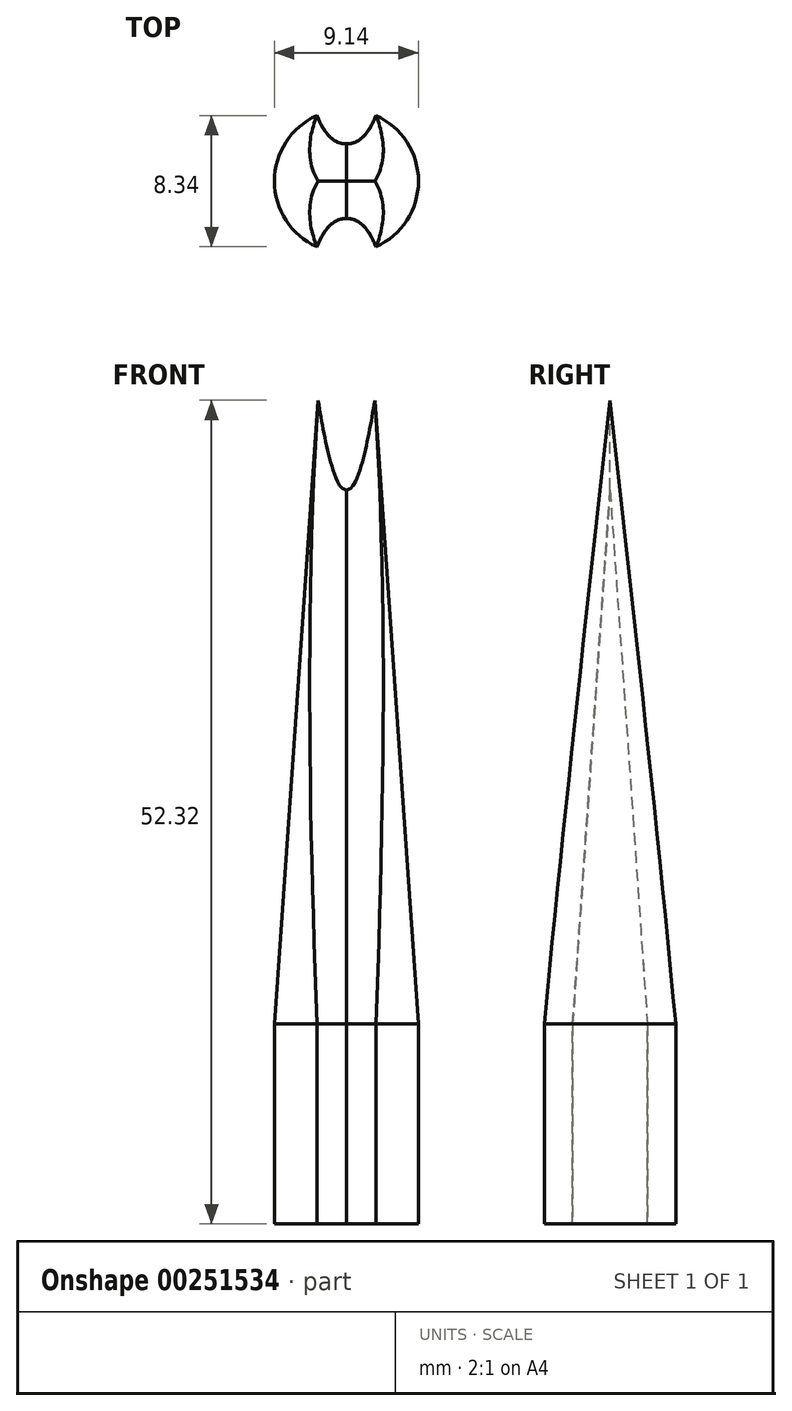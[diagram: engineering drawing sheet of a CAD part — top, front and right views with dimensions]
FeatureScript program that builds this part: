
annotation { "Feature Type Name" : "Feature", "Feature Type Description" : "" }
export const myFeature = defineFeature(function(context is Context, id is Id, definition is map)
    precondition{}
    {
        {
            var Q0;
            Q0=qCreatedBy(makeId("Top.planeOp"),FACE);
            var sketch = newSketch(context, id + "F0", { "sketchPlane" : qUnion([Q0])});
            skArc(sketch, "E0", {"start": v(-1.87, 4.17) * mm, "mid": v(-4.57, 0) * mm, "end": v(-1.87, -4.17) * mm});
            skFitSpline(sketch, "E1", {"points": [v(-1.87, 4.17) * mm, v(0, 2.37) * mm], "startDerivative": vector(1, -2.54) * mm, "endDerivative": vector(2.94, 0.07) * mm});
            skFitSpline(sketch, "E2.MirrorCS", {"points": [v(1.87, 4.17) * mm, v(0, 2.37) * mm], "startDerivative": vector(-1, -2.54) * mm, "endDerivative": vector(-2.94, 0.07) * mm});
            skFitSpline(sketch, "E3.MirrorCS", {"points": [v(-1.87, -4.17) * mm, v(0, -2.37) * mm], "startDerivative": vector(1, 2.54) * mm, "endDerivative": vector(2.94, -0.07) * mm});
            skFitSpline(sketch, "E4.MirrorCS", {"points": [v(1.87, -4.17) * mm, v(0, -2.37) * mm], "startDerivative": vector(-1, 2.54) * mm, "endDerivative": vector(-2.94, -0.07) * mm});
            skFitSpline(sketch, "E5.MirrorCS", {"points": [v(-1.87, -4.17) * mm, v(0, -2.37) * mm], "startDerivative": vector(1, 2.54) * mm, "endDerivative": vector(2.94, -0.07) * mm});
            skArc(sketch, "E6.trimOffspring", {"start": v(1.87, -4.17) * mm, "mid": v(4.57, 0) * mm, "end": v(1.87, 4.17) * mm});
            skSolve(sketch);
        }
        {
            var Q0;
            Q0=makeQuery(id+"F0.imprint","IMPRINT",FACE,{"disambiguationData":[TD([[makeQuery(id+"F0.imprint","IMPRINT",EDGE,{"derivedFrom":sQuery(id+"F0.wireOp",EDGE,"E0")}),1.0]])]});
            extrude(context, id + "F1", {"entities" : qUnion([Q0]), "depth" : 40.9 * mm, "hasDraft" : true, "draftAngle" : 4 * degree, "draftPullDirection" : true});
        }
        {
            var Q0;
            Q0=makeQuery(id+"F1.opExtrude","CAP_FACE",FACE,{"disambiguationData":[OSD([sQuery(id+"F0.wireOp",EDGE,"E0"),sQuery(id+"F0.wireOp",EDGE,"E1"),sQuery(id+"F0.wireOp",EDGE,"E2.MirrorCS"),sQuery(id+"F0.wireOp",EDGE,"E4.MirrorCS"),sQuery(id+"F0.wireOp",EDGE,"E5.MirrorCS"),sQuery(id+"F0.wireOp",EDGE,"E6.trimOffspring")])],"isStart":true});
            extrude(context, id + "F2", {"entities" : qUnion([Q0]), "operationType" : NewBodyOperationType.ADD, "depth" : 12.7 * mm});
        }
    });
